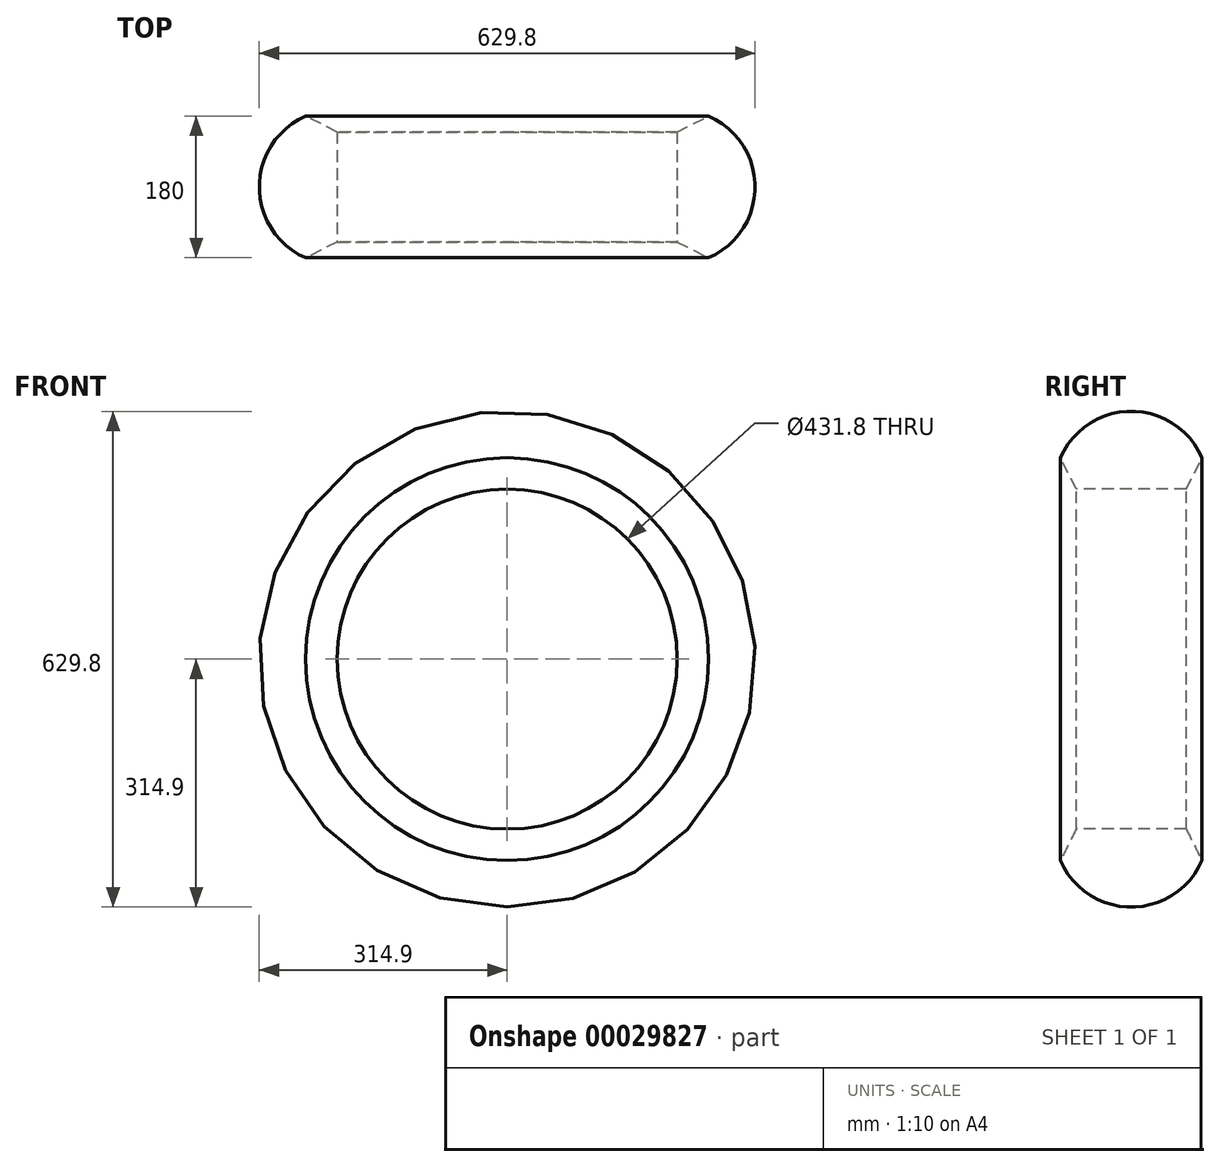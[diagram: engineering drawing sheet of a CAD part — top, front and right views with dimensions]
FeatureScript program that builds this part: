
annotation { "Feature Type Name" : "Feature", "Feature Type Description" : "" }
export const myFeature = defineFeature(function(context is Context, id is Id, definition is map)
    precondition{}
    {
        {
            var Q0;
            Q0=qCreatedBy(makeId("Right.planeOp"),FACE);
            var sketch = newSketch(context, id + "F0", { "sketchPlane" : qUnion([Q0])});
            skArc(sketch, "E0", {"start": v(90, 255.9) * mm, "mid": v(0, 314.9) * mm, "end": v(-90, 255.9) * mm});
            skLineSegment(sketch, "E1", {"start": v(-90, 255.9) * mm, "end": v(-69.85, 215.9) * mm});
            skLineSegment(sketch, "E2", {"start": v(90, 255.9) * mm, "end": v(69.85, 215.9) * mm});
            skLineSegment(sketch, "E3", {"start": v(-69.85, 215.9) * mm, "end": v(69.85, 215.9) * mm});
            skLineSegment(sketch, "E4", {"start": v(0, 0) * mm, "end": v(0, 215.9) * mm, "construction": true});
            skLineSegment(sketch, "E5", {"start": v(-55.35, 0) * mm, "end": v(56.35, 0) * mm, "construction": true});
            skSolve(sketch);
        }
        {
            var Q0;
            Q0=qSketchRegion(id+"F0",true);
            var Q1;
            Q1=sQuery(id+"F0.wireOp",EDGE,"E5");
            revolve(context, id + "F1", {"entities" : qUnion([Q0]), "axis" : qUnion([Q1]), "revolveType" : RevolveType.FULL});
        }
    });
